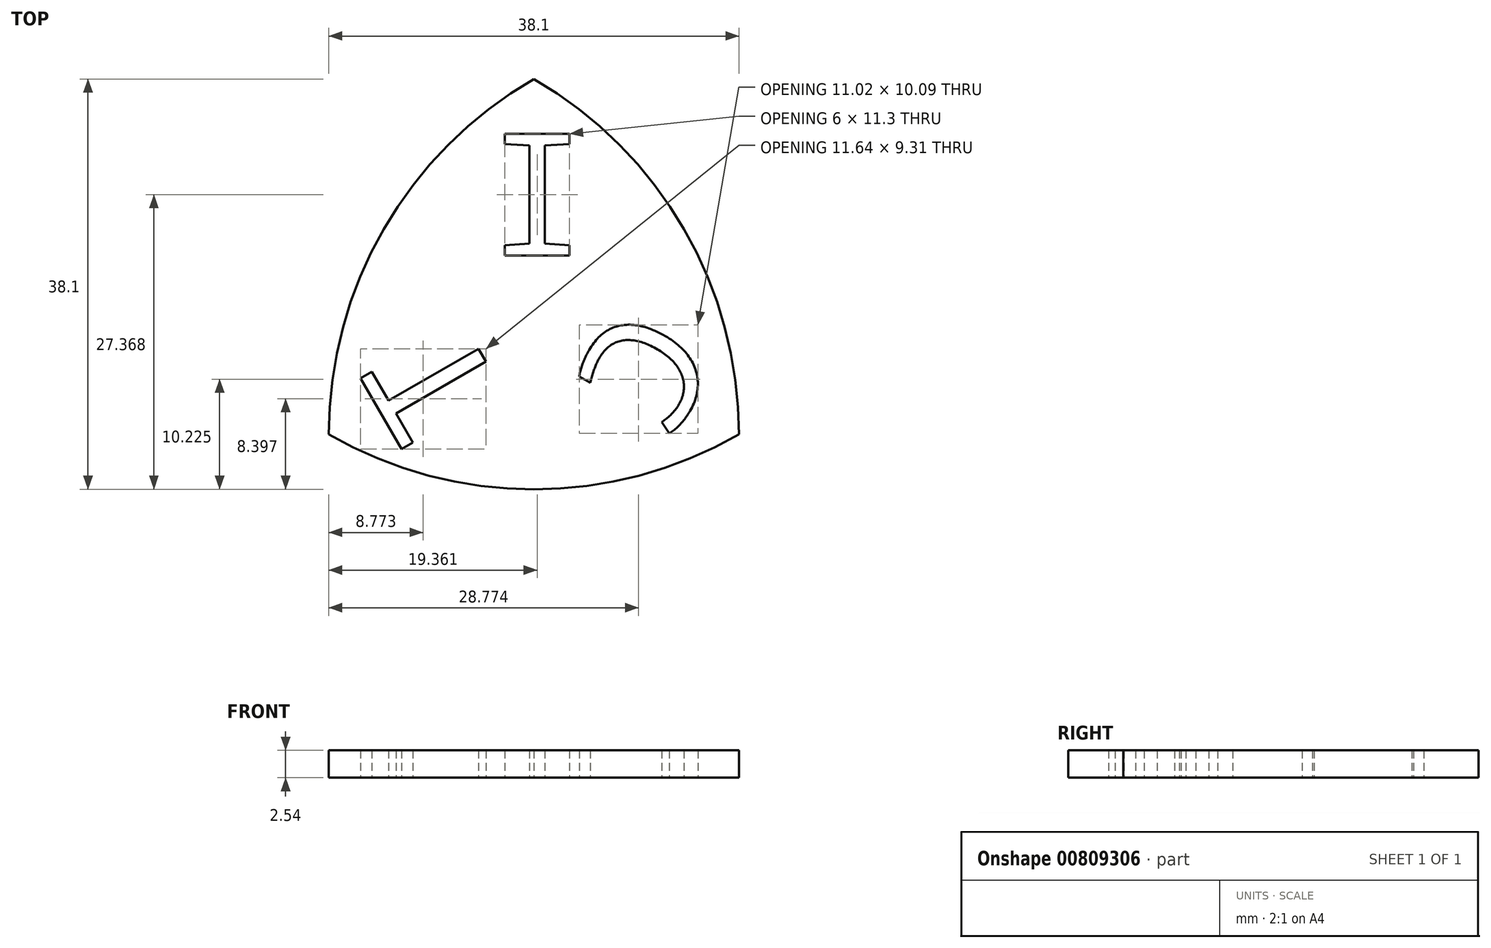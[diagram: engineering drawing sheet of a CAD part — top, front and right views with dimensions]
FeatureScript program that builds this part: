
annotation { "Feature Type Name" : "Feature", "Feature Type Description" : "" }
export const myFeature = defineFeature(function(context is Context, id is Id, definition is map)
    precondition{}
    {
        {
            var Q0;
            Q0=qCreatedBy(makeId("Top.planeOp"),FACE);
            var sketch = newSketch(context, id + "F0", { "sketchPlane" : qUnion([Q0])});
            skCircle(sketch, "E0", {"center": v(0, 0) * mm, "radius": 38.1 * mm});
            skSolve(sketch);
        }
        {
            var Q0;
            Q0=qCreatedBy(makeId("Top.planeOp"),FACE);
            var sketch = newSketch(context, id + "F1", { "sketchPlane" : qUnion([Q0])});
            skCircle(sketch, "E1", {"center": v(-38.1, 0) * mm, "radius": 38.1 * mm});
            skSolve(sketch);
        }
        {
            var Q0;
            Q0=qCreatedBy(makeId("Top.planeOp"),FACE);
            var sketch = newSketch(context, id + "F2", { "sketchPlane" : qUnion([Q0])});
            skCircle(sketch, "E2", {"center": v(-19.05, 33) * mm, "radius": 38.1 * mm});
            skSolve(sketch);
        }
        {
            var Q0;
            Q0 = qSketchRegion(id + "F0", true);
            extrude(context, id + "F3", {"entities" : qUnion([Q0]), "depth" : 2.54 * mm, "offsetDistance" : 25.4 * mm});
        }
        {
            var Q0;
            Q0 = qSketchRegion(id + "F1", true);
            extrude(context, id + "F4", {"entities" : qUnion([Q0]), "depth" : 2.54 * mm, "offsetDistance" : 25.4 * mm});
        }
        {
            var Q0;
            Q0 = qSketchRegion(id + "F2", true);
            extrude(context, id + "F5", {"entities" : qUnion([Q0]), "depth" : 2.54 * mm, "offsetDistance" : 25.4 * mm});
        }
        {
            var Q0;
            Q0=makeQuery(id+"F3.opExtrude","SWEPT_BODY",BODY,{"disambiguationData":[OSD([sQuery(id+"F0.wireOp",EDGE,"E0")])]});
            var Q1;
            Q1=makeQuery(id+"F4.opExtrude","SWEPT_BODY",BODY,{"disambiguationData":[OSD([sQuery(id+"F1.wireOp",EDGE,"E1")])]});
            var Q2;
            Q2=makeQuery(id+"F5.opExtrude","SWEPT_BODY",BODY,{"disambiguationData":[OSD([sQuery(id+"F2.wireOp",EDGE,"E2")])]});
            booleanBodies(context, id + "F6", {"operationType" : BooleanOperationType.INTERSECTION, "tools" : qUnion([Q0, Q1, Q2])});
        }
        {
            var Q0;
            Q0=qCreatedBy(makeId("Top.planeOp"),FACE);
            var sketch = newSketch(context, id + "F7", { "sketchPlane" : qUnion([Q0])});
            skText(sketch, "E3", { "text": "C", "fontName": "DroidSansMono.ttf"});
            skText(sketch, "E4", { "text": "I", "fontName": "DroidSansMono.ttf"});
            skText(sketch, "E5", { "text": "T", "fontName": "DroidSansMono.ttf"});
            const initialGuessF7  = {"E3": [-0.01099, 0.0126, -0.5, -0.86603, 0.01073], "E4": [-0.014, 0.02792, -1, 0, 0.0114], "E5": [-0.02158, 0.00341, -0.5, 0.86603, 0.01094]};
            skSetInitialGuess(sketch, initialGuessF7);
            skSolve(sketch);
        }
        {
            var Q0;
            Q0 = qSketchRegion(id + "F7", true);
            extrude(context, id + "F8", {"entities" : qUnion([Q0]), "depth" : 2.54 * mm, "offsetDistance" : 25.4 * mm});
        }
        {
            var Q0;
            Q0=makeQuery(id+"F8.opExtrude","SWEPT_BODY",BODY,{"disambiguationData":[OSD([sQuery(id+"F7.wireOp",EDGE,"E3.sketch_text.stroke-0"),sQuery(id+"F7.wireOp",EDGE,"E3.sketch_text.stroke-1"),sQuery(id+"F7.wireOp",EDGE,"E3.sketch_text.stroke-2"),sQuery(id+"F7.wireOp",EDGE,"E3.sketch_text.stroke-3"),sQuery(id+"F7.wireOp",EDGE,"E3.sketch_text.stroke-4"),sQuery(id+"F7.wireOp",EDGE,"E3.sketch_text.stroke-5"),sQuery(id+"F7.wireOp",EDGE,"E3.sketch_text.stroke-6"),sQuery(id+"F7.wireOp",EDGE,"E3.sketch_text.stroke-7"),sQuery(id+"F7.wireOp",EDGE,"E3.sketch_text.stroke-8"),sQuery(id+"F7.wireOp",EDGE,"E3.sketch_text.stroke-9"),sQuery(id+"F7.wireOp",EDGE,"E3.sketch_text.stroke-10"),sQuery(id+"F7.wireOp",EDGE,"E3.sketch_text.stroke-11"),sQuery(id+"F7.wireOp",EDGE,"E3.sketch_text.stroke-12"),sQuery(id+"F7.wireOp",EDGE,"E3.sketch_text.stroke-13")])]});
            var Q1;
            Q1=makeQuery(id+"F8.opExtrude","SWEPT_BODY",BODY,{"disambiguationData":[OSD([sQuery(id+"F7.wireOp",EDGE,"E4.sketch_text.stroke-0"),sQuery(id+"F7.wireOp",EDGE,"E4.sketch_text.stroke-1"),sQuery(id+"F7.wireOp",EDGE,"E4.sketch_text.stroke-2"),sQuery(id+"F7.wireOp",EDGE,"E4.sketch_text.stroke-3"),sQuery(id+"F7.wireOp",EDGE,"E4.sketch_text.stroke-4"),sQuery(id+"F7.wireOp",EDGE,"E4.sketch_text.stroke-5"),sQuery(id+"F7.wireOp",EDGE,"E4.sketch_text.stroke-6"),sQuery(id+"F7.wireOp",EDGE,"E4.sketch_text.stroke-7"),sQuery(id+"F7.wireOp",EDGE,"E4.sketch_text.stroke-8"),sQuery(id+"F7.wireOp",EDGE,"E4.sketch_text.stroke-9"),sQuery(id+"F7.wireOp",EDGE,"E4.sketch_text.stroke-10"),sQuery(id+"F7.wireOp",EDGE,"E4.sketch_text.stroke-11"),sQuery(id+"F7.wireOp",EDGE,"E4.sketch_text.stroke-12")])]});
            var Q2;
            Q2=makeQuery(id+"F8.opExtrude","SWEPT_BODY",BODY,{"disambiguationData":[OSD([sQuery(id+"F7.wireOp",EDGE,"E5.sketch_text.stroke-0"),sQuery(id+"F7.wireOp",EDGE,"E5.sketch_text.stroke-1"),sQuery(id+"F7.wireOp",EDGE,"E5.sketch_text.stroke-2"),sQuery(id+"F7.wireOp",EDGE,"E5.sketch_text.stroke-3"),sQuery(id+"F7.wireOp",EDGE,"E5.sketch_text.stroke-4"),sQuery(id+"F7.wireOp",EDGE,"E5.sketch_text.stroke-5"),sQuery(id+"F7.wireOp",EDGE,"E5.sketch_text.stroke-6"),sQuery(id+"F7.wireOp",EDGE,"E5.sketch_text.stroke-7"),sQuery(id+"F7.wireOp",EDGE,"E5.sketch_text.stroke-8"),sQuery(id+"F7.wireOp",EDGE,"E5.sketch_text.stroke-9"),sQuery(id+"F7.wireOp",EDGE,"E5.sketch_text.stroke-10"),sQuery(id+"F7.wireOp",EDGE,"E5.sketch_text.stroke-11"),sQuery(id+"F7.wireOp",EDGE,"E5.sketch_text.stroke-12"),sQuery(id+"F7.wireOp",EDGE,"E5.sketch_text.stroke-13"),sQuery(id+"F7.wireOp",EDGE,"E5.sketch_text.stroke-14"),sQuery(id+"F7.wireOp",EDGE,"E5.sketch_text.stroke-15"),sQuery(id+"F7.wireOp",EDGE,"E5.sketch_text.stroke-16"),sQuery(id+"F7.wireOp",EDGE,"E5.sketch_text.stroke-17")])]});
            var Q3;
            Q3=makeQuery(id+"F6.opBoolean","INTERSECT",BODY,{"derivedFrom":[makeQuery(id+"F3.opExtrude","SWEPT_BODY",BODY,{"disambiguationData":[OSD([sQuery(id+"F0.wireOp",EDGE,"E0")])]}),makeQuery(id+"F4.opExtrude","SWEPT_BODY",BODY,{"disambiguationData":[OSD([sQuery(id+"F1.wireOp",EDGE,"E1")])]}),makeQuery(id+"F5.opExtrude","SWEPT_BODY",BODY,{"disambiguationData":[OSD([sQuery(id+"F2.wireOp",EDGE,"E2")])]})]});
            booleanBodies(context, id + "F9", {"operationType" : BooleanOperationType.SUBTRACTION, "tools" : qUnion([Q0, Q1, Q2]), "targets" : qUnion([Q3])});
        }
    });
